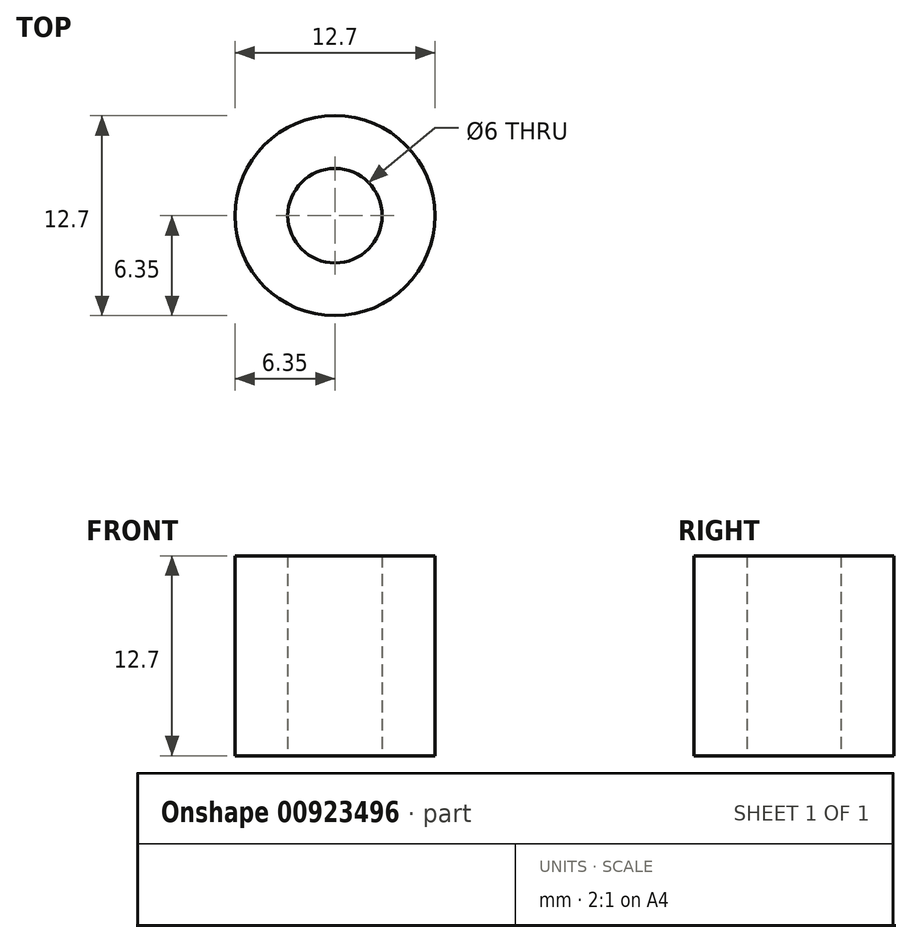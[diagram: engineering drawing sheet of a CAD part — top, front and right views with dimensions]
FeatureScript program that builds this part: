
annotation { "Feature Type Name" : "Feature", "Feature Type Description" : "" }
export const myFeature = defineFeature(function(context is Context, id is Id, definition is map)
    precondition{}
    {
        {
            var Q0;
            Q0=qCreatedBy(makeId("Top.planeOp"),FACE);
            var sketch = newSketch(context, id + "F0", { "sketchPlane" : qUnion([Q0])});
            skCircle(sketch, "E0", {"center": v(0, 0) * mm, "radius": 3 * mm});
            skCircle(sketch, "E1", {"center": v(0, 0) * mm, "radius": 6.35 * mm});
            skCircle(sketch, "E2", {"center": v(0, 0) * mm, "radius": 2.25 * mm, "construction": true});
            skSolve(sketch);
        }
        {
            var Q0;
            Q0=qSketchRegion(id+"F0",true);
            extrude(context, id + "F1", {"entities" : qUnion([Q0]), "depth" : 12.7 * mm, "offsetDistance" : 25 * mm});
        }
    });
